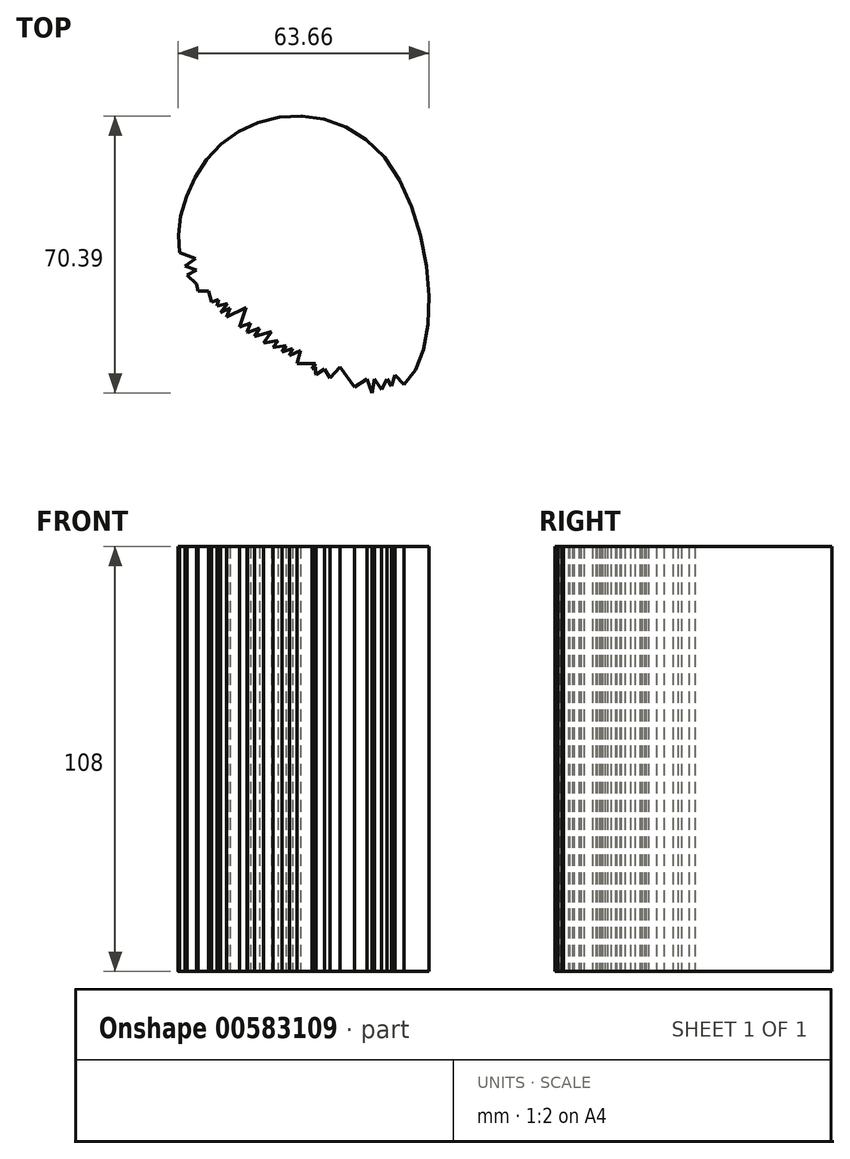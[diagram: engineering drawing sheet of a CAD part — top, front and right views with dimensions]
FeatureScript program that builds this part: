
annotation { "Feature Type Name" : "Feature", "Feature Type Description" : "" }
export const myFeature = defineFeature(function(context is Context, id is Id, definition is map)
    precondition{}
    {
        {
            var Q0;
            Q0=qCreatedBy(makeId("Top.planeOp"),FACE);
            var sketch = newSketch(context, id + "F0", { "sketchPlane" : qUnion([Q0])});
            skFitSpline(sketch, "E0", {"points": [v(0, 0) * mm, v(38.58, -6.43) * mm, v(43.1, -63.6) * mm, v(5.51, -51.8) * mm, v(-13.93, -30.13) * mm, v(0, 0) * mm]});
            skLineSegment(sketch, "E1", {"start": v(-6.83, -49.07) * mm, "end": v(2.98, -44.04) * mm});
            skLineSegment(sketch, "E2", {"start": v(2.98, -44.04) * mm, "end": v(0, -52.95) * mm});
            skLineSegment(sketch, "E3", {"start": v(0, -52.95) * mm, "end": v(2.98, -44.04) * mm});
            skLineSegment(sketch, "E4", {"start": v(-1.56, -50.07) * mm, "end": v(4.1, -48) * mm});
            skLineSegment(sketch, "E5", {"start": v(4.1, -48) * mm, "end": v(2.82, -51.8) * mm});
            skLineSegment(sketch, "E6", {"start": v(1.78, -50.97) * mm, "end": v(6.44, -49.23) * mm});
            skLineSegment(sketch, "E7", {"start": v(6.44, -49.23) * mm, "end": v(4.1, -53.35) * mm});
            skLineSegment(sketch, "E8", {"start": v(-2.39, -48) * mm, "end": v(-1.11, -44.2) * mm});
            skLineSegment(sketch, "E9", {"start": v(-1.11, -44.2) * mm, "end": v(-5.8, -46.57) * mm});
            skLineSegment(sketch, "E10", {"start": v(-5.3, -44.2) * mm, "end": v(-6.55, -39.89) * mm});
            skLineSegment(sketch, "E11", {"start": v(-6.55, -39.89) * mm, "end": v(-10.92, -39.89) * mm});
            skLineSegment(sketch, "E12", {"start": v(-14.93, -32.7) * mm, "end": v(-9.56, -34.5) * mm});
            skLineSegment(sketch, "E13", {"start": v(-9.56, -34.5) * mm, "end": v(-13.37, -36.43) * mm});
            skLineSegment(sketch, "E14", {"start": v(-13.37, -34.5) * mm, "end": v(-9.56, -38.06) * mm});
            skLineSegment(sketch, "E15", {"start": v(-9.56, -38.06) * mm, "end": v(-8.54, -42.3) * mm});
            skLineSegment(sketch, "E16", {"start": v(4.1, -51.8) * mm, "end": v(9.55, -50.1) * mm});
            skLineSegment(sketch, "E17", {"start": v(9.55, -50.1) * mm, "end": v(6.44, -54.5) * mm});
            skLineSegment(sketch, "E18", {"start": v(-6.6, -44.2) * mm, "end": v(-1.7, -43.04) * mm});
            skLineSegment(sketch, "E19", {"start": v(-1.7, -43.04) * mm, "end": v(-3.46, -45.38) * mm});
            skLineSegment(sketch, "E20", {"start": v(-7.93, -43.4) * mm, "end": v(-4.03, -42.04) * mm});
            skPoint(sketch, "E20.endSnap0", {"position": v(-5.93, -42.04) * mm});
            skLineSegment(sketch, "E21", {"start": v(-4.9, -46.11) * mm, "end": v(-4.03, -42.04) * mm});
            skLineSegment(sketch, "E22", {"start": v(5.9, -53.3) * mm, "end": v(11.09, -52.46) * mm});
            skLineSegment(sketch, "E23", {"start": v(8.54, -56) * mm, "end": v(11.09, -52.46) * mm});
            skLineSegment(sketch, "E24", {"start": v(8.24, -54.5) * mm, "end": v(13.21, -53.7) * mm});
            skLineSegment(sketch, "E25", {"start": v(11.2, -56.96) * mm, "end": v(13.21, -53.7) * mm});
            skLineSegment(sketch, "E26", {"start": v(10, -56) * mm, "end": v(14.83, -54.5) * mm});
            skLineSegment(sketch, "E27", {"start": v(13.21, -58.35) * mm, "end": v(14.83, -54.5) * mm});
            skLineSegment(sketch, "E28", {"start": v(12.25, -57.08) * mm, "end": v(16.86, -55.01) * mm});
            skLineSegment(sketch, "E29", {"start": v(15.61, -59.96) * mm, "end": v(16.86, -55.01) * mm});
            skLineSegment(sketch, "E30", {"start": v(14.82, -58.35) * mm, "end": v(20.61, -58.35) * mm});
            skLineSegment(sketch, "E31", {"start": v(18.28, -62.25) * mm, "end": v(20.61, -58.35) * mm});
            skLineSegment(sketch, "E32", {"start": v(18.28, -60.68) * mm, "end": v(20.61, -59.18) * mm});
            skLineSegment(sketch, "E33", {"start": v(20.61, -62.98) * mm, "end": v(20.61, -59.18) * mm});
            skLineSegment(sketch, "E34", {"start": v(19.65, -61.79) * mm, "end": v(22.92, -59.68) * mm});
            skLineSegment(sketch, "E35", {"start": v(26.85, -66) * mm, "end": v(22.92, -59.68) * mm});
            skLineSegment(sketch, "E36", {"start": v(22.92, -63.7) * mm, "end": v(26.85, -59.18) * mm});
            skLineSegment(sketch, "E37", {"start": v(32.66, -67.17) * mm, "end": v(26.85, -59.18) * mm});
            skLineSegment(sketch, "E38", {"start": v(33.7, -62.25) * mm, "end": v(29.8, -64.77) * mm});
            skLineSegment(sketch, "E39", {"start": v(29.8, -64.77) * mm, "end": v(27.88, -66) * mm});
            skLineSegment(sketch, "E40", {"start": v(33.7, -62.25) * mm, "end": v(35.7, -67.61) * mm});
            skLineSegment(sketch, "E41", {"start": v(35.7, -67.61) * mm, "end": v(35.02, -65.77) * mm});
            skLineSegment(sketch, "E42", {"start": v(35.02, -65.77) * mm, "end": v(35.7, -62.25) * mm});
            skLineSegment(sketch, "E43", {"start": v(35.7, -62.25) * mm, "end": v(37.93, -65.7) * mm});
            skLineSegment(sketch, "E44", {"start": v(37.93, -65.7) * mm, "end": v(36.62, -66.55) * mm});
            skLineSegment(sketch, "E45", {"start": v(36.62, -66.55) * mm, "end": v(38.81, -62.25) * mm});
            skLineSegment(sketch, "E46", {"start": v(38.81, -62.25) * mm, "end": v(42.27, -67.61) * mm});
            skLineSegment(sketch, "E47", {"start": v(43.1, -63.6) * mm, "end": v(40.87, -61.27) * mm});
            skLineSegment(sketch, "E48", {"start": v(38.85, -67.18) * mm, "end": v(40.87, -61.27) * mm});
            skLineSegment(sketch, "E49", {"start": v(-13.93, -30.13) * mm, "end": v(-9.85, -31.64) * mm});
            skLineSegment(sketch, "E50", {"start": v(-9.85, -31.64) * mm, "end": v(-14.97, -35.4) * mm});
            skSolve(sketch);
        }
        {
            var Q0;
            {var subQ72=sQuery(id+"F0.wireOp",EDGE,"E19");Q0=makeQuery(id+"F0.imprint","IMPRINT",FACE,{"disambiguationData":[TD([[makeQuery(id+"F0.imprint","IMPRINT",EDGE,{"derivedFrom":subQ72}),1.0]])]});}
            extrude(context, id + "F1", {"entities" : qUnion([Q0]), "depth" : 108 * mm, "offsetDistance" : 25 * mm});
        }
    });
